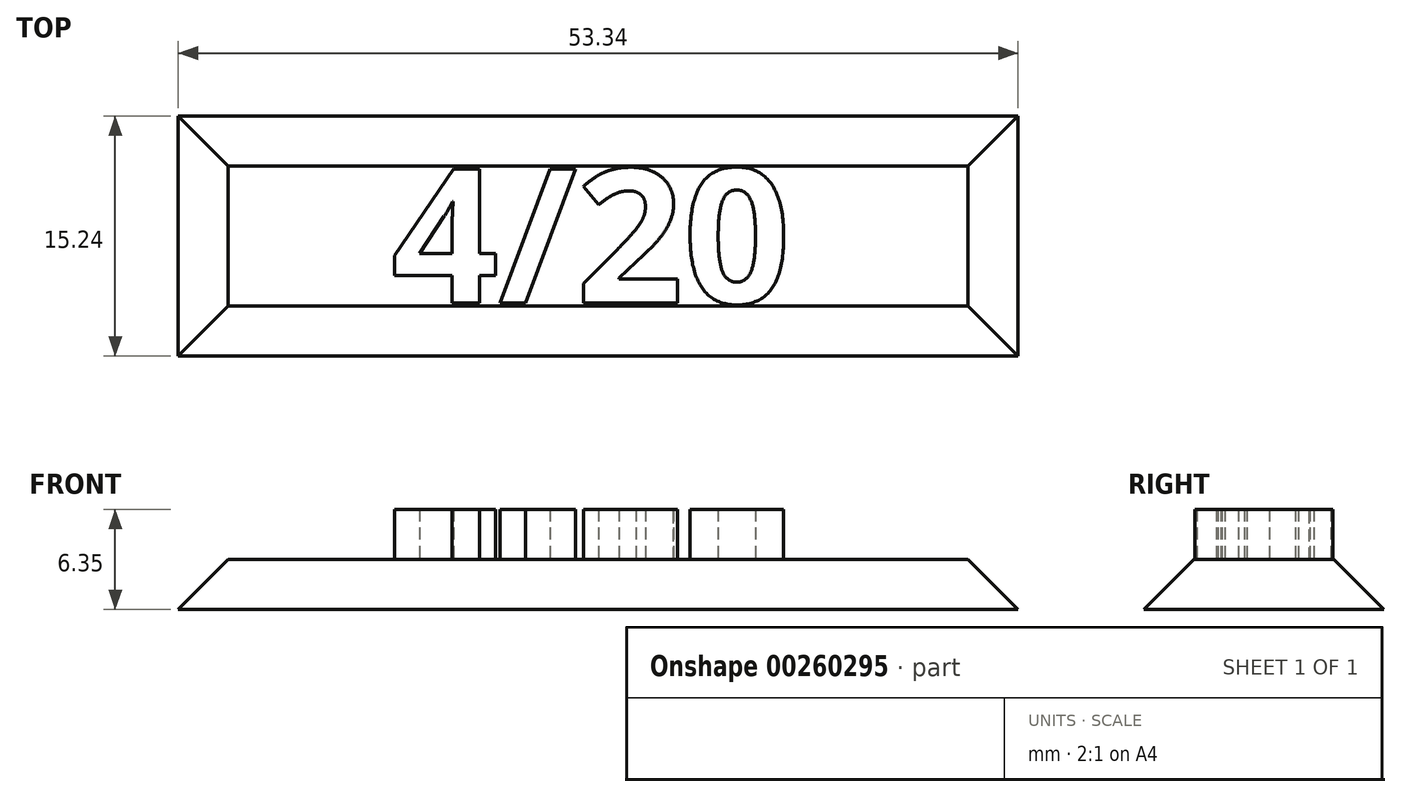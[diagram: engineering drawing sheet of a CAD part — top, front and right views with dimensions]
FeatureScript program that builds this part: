
annotation { "Feature Type Name" : "Feature", "Feature Type Description" : "" }
export const myFeature = defineFeature(function(context is Context, id is Id, definition is map)
    precondition{}
    {
        {
            var Q0;
            Q0=qCreatedBy(makeId("Top.planeOp"),FACE);
            var sketch = newSketch(context, id + "F0", { "sketchPlane" : qUnion([Q0])});
            skLineSegment(sketch, "E0.bottom", {"start": v(-26.68, 7.96) * mm, "end": v(30.47, 7.96) * mm});
            skLineSegment(sketch, "E0.top", {"start": v(-26.68, -11.1) * mm, "end": v(30.47, -11.1) * mm});
            skLineSegment(sketch, "E0.left", {"start": v(-26.68, 7.96) * mm, "end": v(-26.68, -11.1) * mm});
            skLineSegment(sketch, "E0.right", {"start": v(30.47, 7.96) * mm, "end": v(30.47, -11.1) * mm});
            skSolve(sketch);
        }
        {
            var Q0;
            Q0 = qSketchRegion(id + "F0", true);
            extrude(context, id + "F1", {"entities" : qUnion([Q0]), "depth" : 3.17 * mm});
        }
        {
            var Q0;
            Q0=makeQuery(id+"F1.opExtrude","CAP_FACE",FACE,{"disambiguationData":[OSD([sQuery(id+"F0.wireOp",EDGE,"E0.bottom"),sQuery(id+"F0.wireOp",EDGE,"E0.top"),sQuery(id+"F0.wireOp",EDGE,"E0.left"),sQuery(id+"F0.wireOp",EDGE,"E0.right")])],"isStart":false});
            chamfer(context, id + "F2", {"entities" : qUnion([Q0]), "width" : 5.08 * mm, "tangentPropagation" : true});
        }
        {
            var Q0;
            Q0=qCreatedBy(makeId("Top.planeOp"),FACE);
            var sketch = newSketch(context, id + "F3", { "sketchPlane" : qUnion([Q0])});
            skText(sketch, "E1", { "text": "4/20", "fontName": "OpenSans-Bold.ttf"});
            const initialGuessF3  = {"E1": [-0.01123, -0.00583, 1, 0, 0.00858]};
            skSetInitialGuess(sketch, initialGuessF3);
            skSolve(sketch);
        }
        {
            var Q0;
            Q0 = qSketchRegion(id + "F3", true);
            extrude(context, id + "F4", {"entities" : qUnion([Q0]), "operationType" : NewBodyOperationType.ADD, "depth" : 6.35 * mm});
        }
    });
